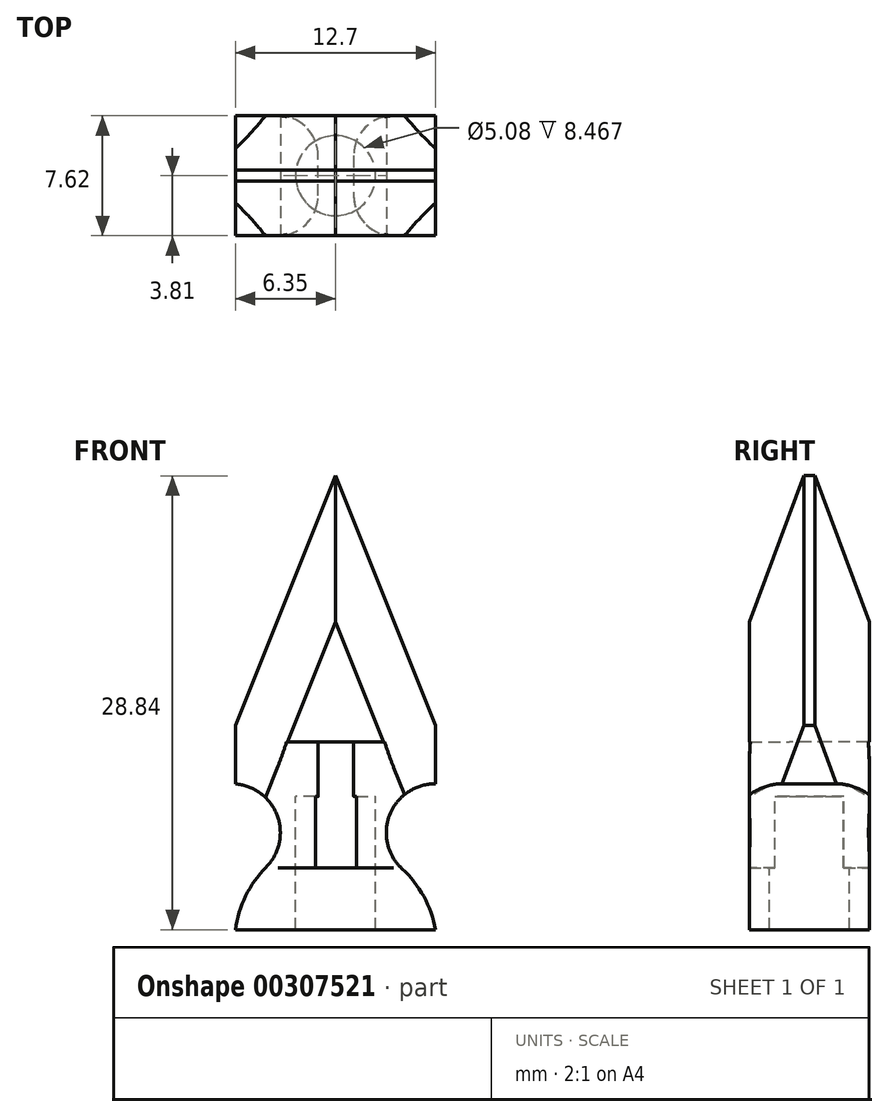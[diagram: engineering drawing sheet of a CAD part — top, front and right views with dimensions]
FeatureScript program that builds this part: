
annotation { "Feature Type Name" : "Feature", "Feature Type Description" : "" }
export const myFeature = defineFeature(function(context is Context, id is Id, definition is map)
    precondition{}
    {
        {
            var Q0;
            Q0=qCreatedBy(makeId("Front.planeOp"),FACE);
            var sketch = newSketch(context, id + "F0", { "sketchPlane" : qUnion([Q0])});
            skLineSegment(sketch, "E0", {"start": v(-6.35, -8.47) * mm, "end": v(-6.35, 4.5) * mm});
            skLineSegment(sketch, "E1", {"start": v(-6.35, 4.5) * mm, "end": v(0, 20.37) * mm});
            skLineSegment(sketch, "E2", {"start": v(0, 20.37) * mm, "end": v(6.35, 4.5) * mm});
            skLineSegment(sketch, "E3", {"start": v(6.35, 4.5) * mm, "end": v(6.35, -8.47) * mm});
            skLineSegment(sketch, "E4", {"start": v(6.35, -8.47) * mm, "end": v(-6.35, -8.47) * mm});
            skSolve(sketch);
        }
        {
            var Q0;
            Q0 = qSketchRegion(id + "F0", true);
            extrude(context, id + "F1", {"entities" : qUnion([Q0]), "depth" : 3.8 * mm, "hasSecondDirection" : true, "secondDirectionOppositeDirection" : true, "secondDirectionDepth" : 3.8 * mm});
        }
        {
            var Q0;
            Q0=qCreatedBy(makeId("Front.planeOp"),FACE);
            var sketch = newSketch(context, id + "F2", { "sketchPlane" : qUnion([Q0])});
            skCircle(sketch, "E5", {"center": v(6.33, -2.3) * mm, "radius": 3.11 * mm});
            skCircle(sketch, "E6", {"center": v(-6.62, -2.3) * mm, "radius": 3.11 * mm});
            skSolve(sketch);
        }
        {
            var Q0;
            Q0 = qSketchRegion(id + "F2", true);
            extrude(context, id + "F3", {"entities" : qUnion([Q0]), "operationType" : NewBodyOperationType.REMOVE, "oppositeDirection" : true, "depth" : 25.4 * mm, "hasSecondDirection" : true, "secondDirectionOppositeDirection" : false, "secondDirectionDepth" : 25.4 * mm});
        }
        {
            var Q0;
            Q0=makeQuery(id+"F1.opExtrude","CAP_EDGE",EDGE,{"disambiguationData":[OSD([sQuery(id+"F0.wireOp",EDGE,"E2")])],"isStart":false});
            var Q1;
            Q1=makeQuery(id+"F1.opExtrude","CAP_EDGE",EDGE,{"disambiguationData":[OSD([sQuery(id+"F0.wireOp",EDGE,"E1")])],"isStart":false});
            var Q2;
            Q2=makeQuery(id+"F1.opExtrude","CAP_EDGE",EDGE,{"disambiguationData":[OSD([sQuery(id+"F0.wireOp",EDGE,"E1")])],"isStart":true});
            var Q3;
            Q3=makeQuery(id+"F1.opExtrude","CAP_EDGE",EDGE,{"disambiguationData":[OSD([sQuery(id+"F0.wireOp",EDGE,"E2")])],"isStart":true});
            chamfer(context, id + "F4", {"entities" : qUnion([Q0, Q1, Q2, Q3]), "width" : 3.45 * mm, "tangentPropagation" : true});
        }
        {
            var Q0;
            Q0=makeQuery(id+"F3.boolean.opBoolean","INTERSECT",EDGE,{"disambiguationData":[OD(0.0)],"derivedFrom":[makeQuery(id+"F1.opExtrude","SWEPT_FACE",FACE,{"disambiguationData":[OSD([sQuery(id+"F0.wireOp",EDGE,"E0")])]}),makeQuery(id+"F3.opExtrude","SWEPT_FACE",FACE,{"disambiguationData":[OSD([sQuery(id+"F2.wireOp",EDGE,"E6")])]})]});
            var Q1;
            Q1=makeQuery(id+"F3.boolean.opBoolean","INTERSECT",EDGE,{"disambiguationData":[OD(1.0)],"derivedFrom":[makeQuery(id+"F1.opExtrude","SWEPT_FACE",FACE,{"disambiguationData":[OSD([sQuery(id+"F0.wireOp",EDGE,"E3")])]}),makeQuery(id+"F3.opExtrude","SWEPT_FACE",FACE,{"disambiguationData":[OSD([sQuery(id+"F2.wireOp",EDGE,"E5")])]})]});
            fillet(context, id + "F5", {"entities" : qUnion([Q0, Q1]), "radius" : 6.92 * mm, "tangentPropagation" : true, "allowEdgeOverflow" : false});
        }
        {
            var Q0;
            Q0=qCreatedBy(makeId("Top.planeOp"),FACE);
            var sketch = newSketch(context, id + "F6", { "sketchPlane" : qUnion([Q0])});
            skCircle(sketch, "E7", {"center": v(0, 0) * mm, "radius": 2.54 * mm});
            skSolve(sketch);
        }
        {
            var Q0;
            Q0 = qSketchRegion(id + "F6", true);
            extrude(context, id + "F7", {"entities" : qUnion([Q0]), "operationType" : NewBodyOperationType.REMOVE, "oppositeDirection" : true, "depth" : 25.4 * mm});
        }
        {
            var Q0;
            Q0=qCreatedBy(makeId("Front.planeOp"),FACE);
            var sketch = newSketch(context, id + "F8", { "sketchPlane" : qUnion([Q0])});
            skLineSegment(sketch, "E8", {"start": v(0, 3.45) * mm, "end": v(1.15, 3.45) * mm});
            skLineSegment(sketch, "E9", {"start": v(1.15, 3.45) * mm, "end": v(1.15, -4.53) * mm});
            skLineSegment(sketch, "E10", {"start": v(1.15, -4.53) * mm, "end": v(0, -4.53) * mm});
            skLineSegment(sketch, "E11", {"start": v(0, -4.53) * mm, "end": v(-1.11, -4.53) * mm});
            skLineSegment(sketch, "E12", {"start": v(-1.11, -4.53) * mm, "end": v(-1.11, 3.45) * mm});
            skLineSegment(sketch, "E13", {"start": v(-1.11, 3.45) * mm, "end": v(0, 3.45) * mm});
            skSolve(sketch);
        }
        {
            var Q0;
            Q0 = qSketchRegion(id + "F8", true);
            extrude(context, id + "F9", {"entities" : qUnion([Q0]), "operationType" : NewBodyOperationType.REMOVE, "oppositeDirection" : true, "depth" : 25.4 * mm, "hasSecondDirection" : true, "secondDirectionOppositeDirection" : false, "secondDirectionDepth" : 25.4 * mm});
        }
        {
            var Q0;
            Q0=makeQuery(id+"F9.boolean.opBoolean","INTERSECT",EDGE,{"derivedFrom":[makeQuery(id+"F1.opExtrude","CAP_FACE",FACE,{"disambiguationData":[OSD([sQuery(id+"F0.wireOp",EDGE,"E0"),sQuery(id+"F0.wireOp",EDGE,"E1"),sQuery(id+"F0.wireOp",EDGE,"E2"),sQuery(id+"F0.wireOp",EDGE,"E3"),sQuery(id+"F0.wireOp",EDGE,"E4")])],"isStart":false}),makeQuery(id+"F9.opExtrude","SWEPT_FACE",FACE,{"disambiguationData":[OSD([sQuery(id+"F8.wireOp",EDGE,"E9")])]})]});
            var Q1;
            Q1=makeQuery(id+"F9.boolean.opBoolean","INTERSECT",EDGE,{"derivedFrom":[makeQuery(id+"F1.opExtrude","CAP_FACE",FACE,{"disambiguationData":[OSD([sQuery(id+"F0.wireOp",EDGE,"E0"),sQuery(id+"F0.wireOp",EDGE,"E1"),sQuery(id+"F0.wireOp",EDGE,"E2"),sQuery(id+"F0.wireOp",EDGE,"E3"),sQuery(id+"F0.wireOp",EDGE,"E4")])],"isStart":true}),makeQuery(id+"F9.opExtrude","SWEPT_FACE",FACE,{"disambiguationData":[OSD([sQuery(id+"F8.wireOp",EDGE,"E12")])]})]});
            var Q2;
            Q2=makeQuery(id+"F9.boolean.opBoolean","INTERSECT",EDGE,{"derivedFrom":[makeQuery(id+"F1.opExtrude","CAP_FACE",FACE,{"disambiguationData":[OSD([sQuery(id+"F0.wireOp",EDGE,"E0"),sQuery(id+"F0.wireOp",EDGE,"E1"),sQuery(id+"F0.wireOp",EDGE,"E2"),sQuery(id+"F0.wireOp",EDGE,"E3"),sQuery(id+"F0.wireOp",EDGE,"E4")])],"isStart":false}),makeQuery(id+"F9.opExtrude","SWEPT_FACE",FACE,{"disambiguationData":[OSD([sQuery(id+"F8.wireOp",EDGE,"E12")])]})]});
            var Q3;
            Q3=makeQuery(id+"F9.boolean.opBoolean","INTERSECT",EDGE,{"derivedFrom":[makeQuery(id+"F1.opExtrude","CAP_FACE",FACE,{"disambiguationData":[OSD([sQuery(id+"F0.wireOp",EDGE,"E0"),sQuery(id+"F0.wireOp",EDGE,"E1"),sQuery(id+"F0.wireOp",EDGE,"E2"),sQuery(id+"F0.wireOp",EDGE,"E3"),sQuery(id+"F0.wireOp",EDGE,"E4")])],"isStart":true}),makeQuery(id+"F9.opExtrude","SWEPT_FACE",FACE,{"disambiguationData":[OSD([sQuery(id+"F8.wireOp",EDGE,"E9")])]})]});
            fillet(context, id + "F10", {"entities" : qUnion([Q0, Q1, Q2, Q3]), "radius" : 2.54 * mm, "tangentPropagation" : true, "allowEdgeOverflow" : false});
        }
    });
